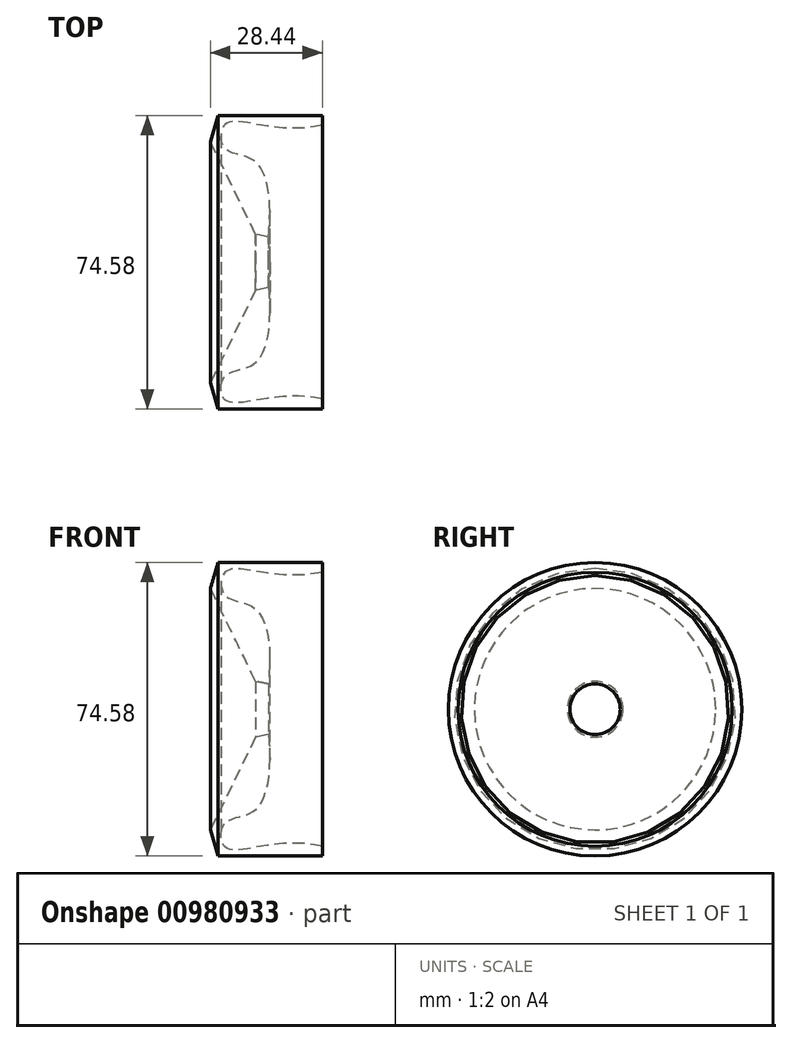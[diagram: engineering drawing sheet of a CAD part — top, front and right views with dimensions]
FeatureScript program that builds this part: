
annotation { "Feature Type Name" : "Feature", "Feature Type Description" : "" }
export const myFeature = defineFeature(function(context is Context, id is Id, definition is map)
    precondition{}
    {
        {
            var Q0;
            Q0=qCreatedBy(makeId("Front.planeOp"),FACE);
            var sketch = newSketch(context, id + "F0", { "sketchPlane" : qUnion([Q0])});
            skFitSpline(sketch, "E0", {"points": [v(-9.42, 34.8) * mm, v(-33.99, 35.08) * mm, v(-34.26, 29.07) * mm, v(-27.16, 26.07) * mm, v(-23.07, 17.6) * mm, v(-23.07, 6.42) * mm], "startDerivative": vector(-123.4, -27.42) * mm, "endDerivative": vector(-3.94, -55.41) * mm});
            skLineSegment(sketch, "E1", {"start": v(-50.37, 0) * mm, "end": v(57.74, 0) * mm, "construction": true});
            skLineSegment(sketch, "E2", {"start": v(-9.42, 34.8) * mm, "end": v(-9.42, 37.29) * mm});
            skLineSegment(sketch, "E3", {"start": v(-9.42, 37.29) * mm, "end": v(-35.9, 37.29) * mm});
            skLineSegment(sketch, "E4", {"start": v(-35.9, 37.29) * mm, "end": v(-37.86, 30.66) * mm});
            skLineSegment(sketch, "E5", {"start": v(-37.86, 30.66) * mm, "end": v(-26.36, 7.08) * mm});
            skLineSegment(sketch, "E6", {"start": v(-26.36, 7.08) * mm, "end": v(-23.07, 6.42) * mm});
            skSolve(sketch);
        }
        {
            var Q0;
            Q0 = qSketchRegion(id + "F0", true);
            var Q1;
            Q1=sQuery(id+"F0.wireOp",EDGE,"E1");
            revolve(context, id + "F1", {"surfaceOperationType" : NewSurfaceOperationType.NEW, "entities" : qUnion([Q0]), "axis" : qUnion([Q1]), "revolveType" : RevolveType.FULL});
        }
    });
